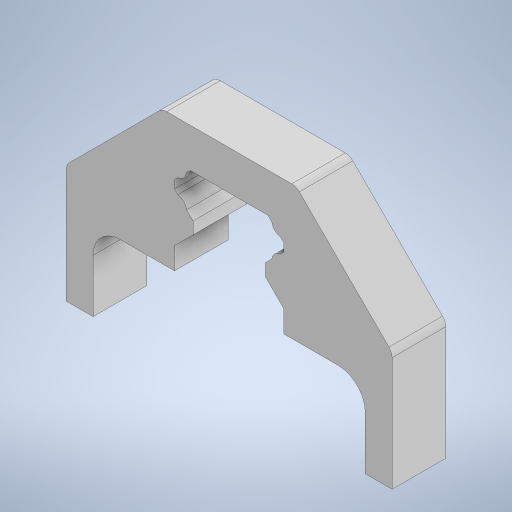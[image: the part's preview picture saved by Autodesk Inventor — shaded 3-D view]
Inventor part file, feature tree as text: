
AUTODESK INVENTOR PART (.ipt)
format: ipt  version: 2023 (Build 270158000, 158)  size: 312,832 bytes
history: native  units: mm
features: extrude x2, sketch x2, fillet x1, thicken_offset x1, projected_geometry x1
ambient origin geometry x8: Origin, YZ Plane, XZ Plane, XY Plane, X Axis, Y Axis, Z Axis, Center Point
bodies: Solid1 (feature_tree)
feature tree (7):
  extrude  "Extrusion1"  Depth=25.0mm
  fillet  "Fillet1"  Radius=60.8mm
  thicken_offset  "Thicken1"
  sketch  "Sketch1"  dims[d0=10.0mm d1=0.0mm]
  projected_geometry  "Projected Loop1"
  extrude  "Extrusion2"  Depth=50.8mm
  sketch  "Sketch2"  dims[d2=15.4mm d3=2.0mm d4=7.16mm d5=2.375mm d6=1.333333mm d7=2.4211mm d8=17.5mm d9=135.0deg d10=3.45mm d11=3.0mm d12=10.0mm d13=1.0mm d15=0.0mm d16=10.0mm d17=25.0mm d18=60.8mm d19=50.8mm d20=15.0mm d21=5.08mm d22=25.0mm d23=45.0deg d24=2.0mm d25=0.2mm d26=0.3mm]
